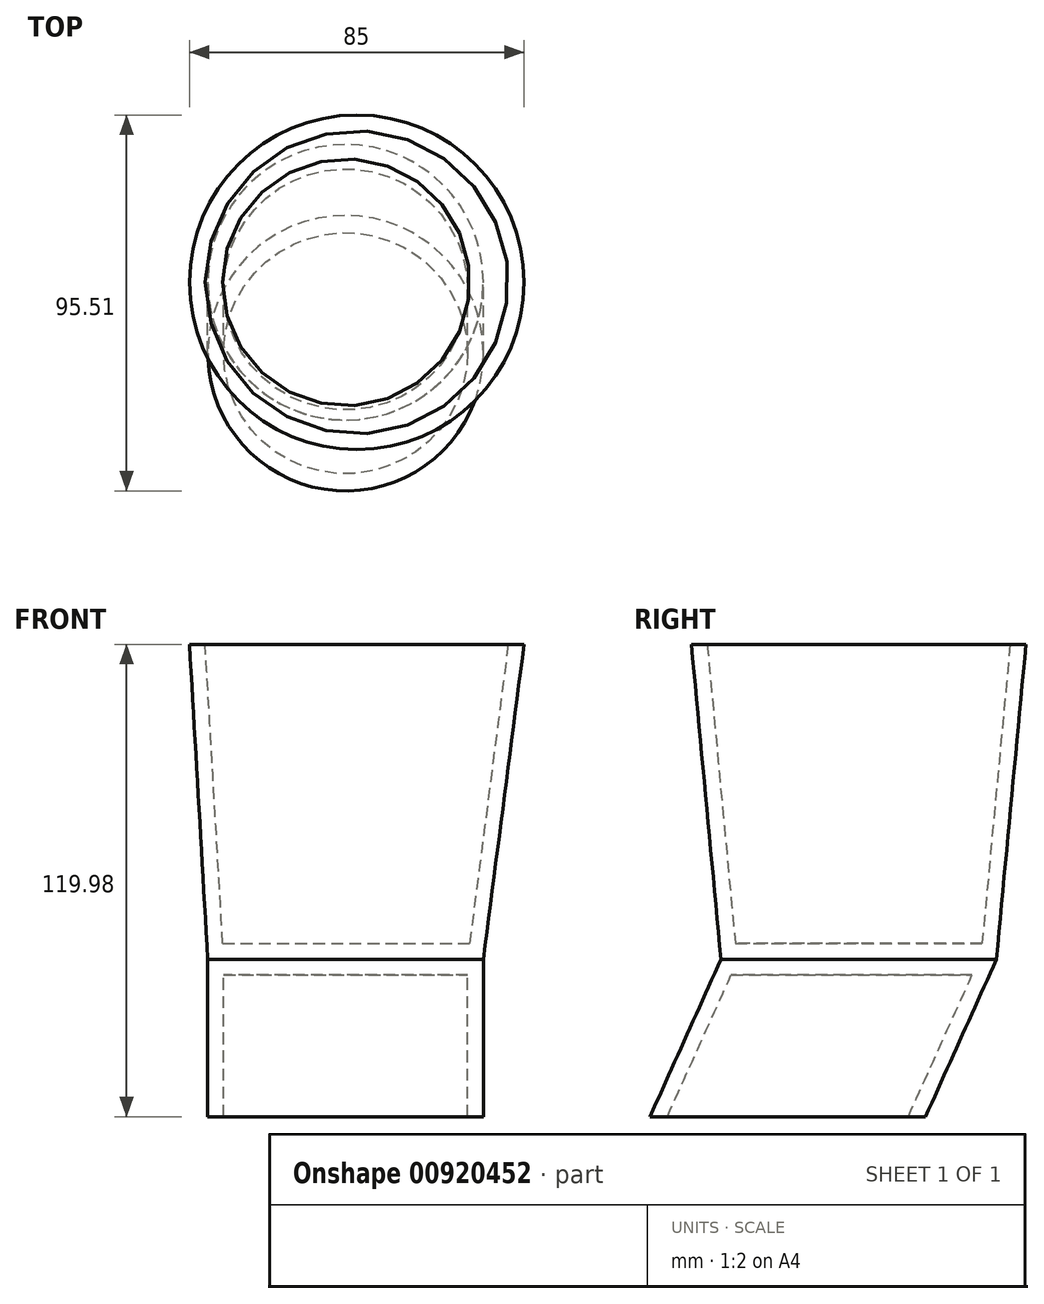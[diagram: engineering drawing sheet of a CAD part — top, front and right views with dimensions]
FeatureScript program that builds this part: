
annotation { "Feature Type Name" : "Feature", "Feature Type Description" : "" }
export const myFeature = defineFeature(function(context is Context, id is Id, definition is map)
    precondition{}
    {
        {
            var Q0;
            Q0=qCreatedBy(makeId("Top.planeOp"),FACE);
            var sketch = newSketch(context, id + "F0", { "sketchPlane" : qUnion([Q0])});
            skCircle(sketch, "E0", {"center": v(0, 0) * mm, "radius": 35 * mm});
            skSolve(sketch);
        }
        {
            var Q0;
            Q0=qCreatedBy(makeId("Top.planeOp"),FACE);
            cPlane(context, id + "F1", {"entities" : qUnion([Q0]), "cplaneType" : CPlaneType.OFFSET, "offset" : 80 * mm, "width" : 150 * mm, "height" : 150 * mm});
        }
        {
            var Q0;
            Q0=qCreatedBy(id+"F1.planeOp",FACE);
            var sketch = newSketch(context, id + "F2", { "sketchPlane" : qUnion([Q0])});
            skCircle(sketch, "E1", {"center": v(2.84, 0) * mm, "radius": 42.5 * mm});
            skSolve(sketch);
        }
        {
            var Q0;
            Q0 = qSketchRegion(id + "F0", true);
            var Q1;
            Q1 = qSketchRegion(id + "F2", true);
            loft(context, id + "F3", {"sheetProfilesArray" : [{ "sheetProfileEntities" : qUnion([Q0]) }, { "sheetProfileEntities" : qUnion([Q1]) }]});
        }
        {
            var Q0;
            Q0=makeQuery(id+"F3.opLoft","CAP_FACE",FACE,{"disambiguationData":[OSD([makeQuery(id+"F2.imprint","IMPRINT",FACE,{"disambiguationData":[TD([[makeQuery(id+"F2.imprint","IMPRINT",EDGE,{"derivedFrom":sQuery(id+"F2.wireOp",EDGE,"E1")}),1.0]])]})])],"isStart":true});
            shell(context, id + "F4", {"entities" : qUnion([Q0]), "thickness" : 4 * mm});
        }
        {
            var Q0;
            Q0=qCreatedBy(makeId("Right.planeOp"),FACE);
            var sketch = newSketch(context, id + "F5", { "sketchPlane" : qUnion([Q0])});
            skLineSegment(sketch, "E2", {"start": v(-35.39, 0) * mm, "end": v(-53.4, -39.98) * mm});
            skLineSegment(sketch, "E3", {"start": v(-53.4, -39.98) * mm, "end": v(-29.4, -74.88) * mm});
            skSolve(sketch);
        }
        {
            var Q0;
            Q0=makeQuery(id+"F3.opLoft","CAP_FACE",FACE,{"disambiguationData":[OSD([makeQuery(id+"F0.imprint","IMPRINT",FACE,{"disambiguationData":[TD([[makeQuery(id+"F0.imprint","IMPRINT",EDGE,{"derivedFrom":sQuery(id+"F0.wireOp",EDGE,"E0")}),1.0]])]})])],"isStart":true});
            var Q1;
            Q1=sQuery(id+"F5.wireOp",EDGE,"E2");
            sweep(context, id + "F6", {"profiles" : qUnion([Q0]), "path" : qUnion([Q1])});
        }
        {
            var Q0;
            Q0=makeQuery(id+"F6.opSweep","CAP_FACE",FACE,{"disambiguationData":[OSD([makeQuery(id+"F0.imprint","IMPRINT",FACE,{"disambiguationData":[TD([[makeQuery(id+"F0.imprint","IMPRINT",EDGE,{"derivedFrom":sQuery(id+"F0.wireOp",EDGE,"E0")}),1.0]])]}),sQuery(id+"F5.wireOp",VERTEX,"E2.end")])],"isStart":false});
            shell(context, id + "F7", {"entities" : qUnion([Q0]), "thickness" : 4 * mm});
        }
    });
